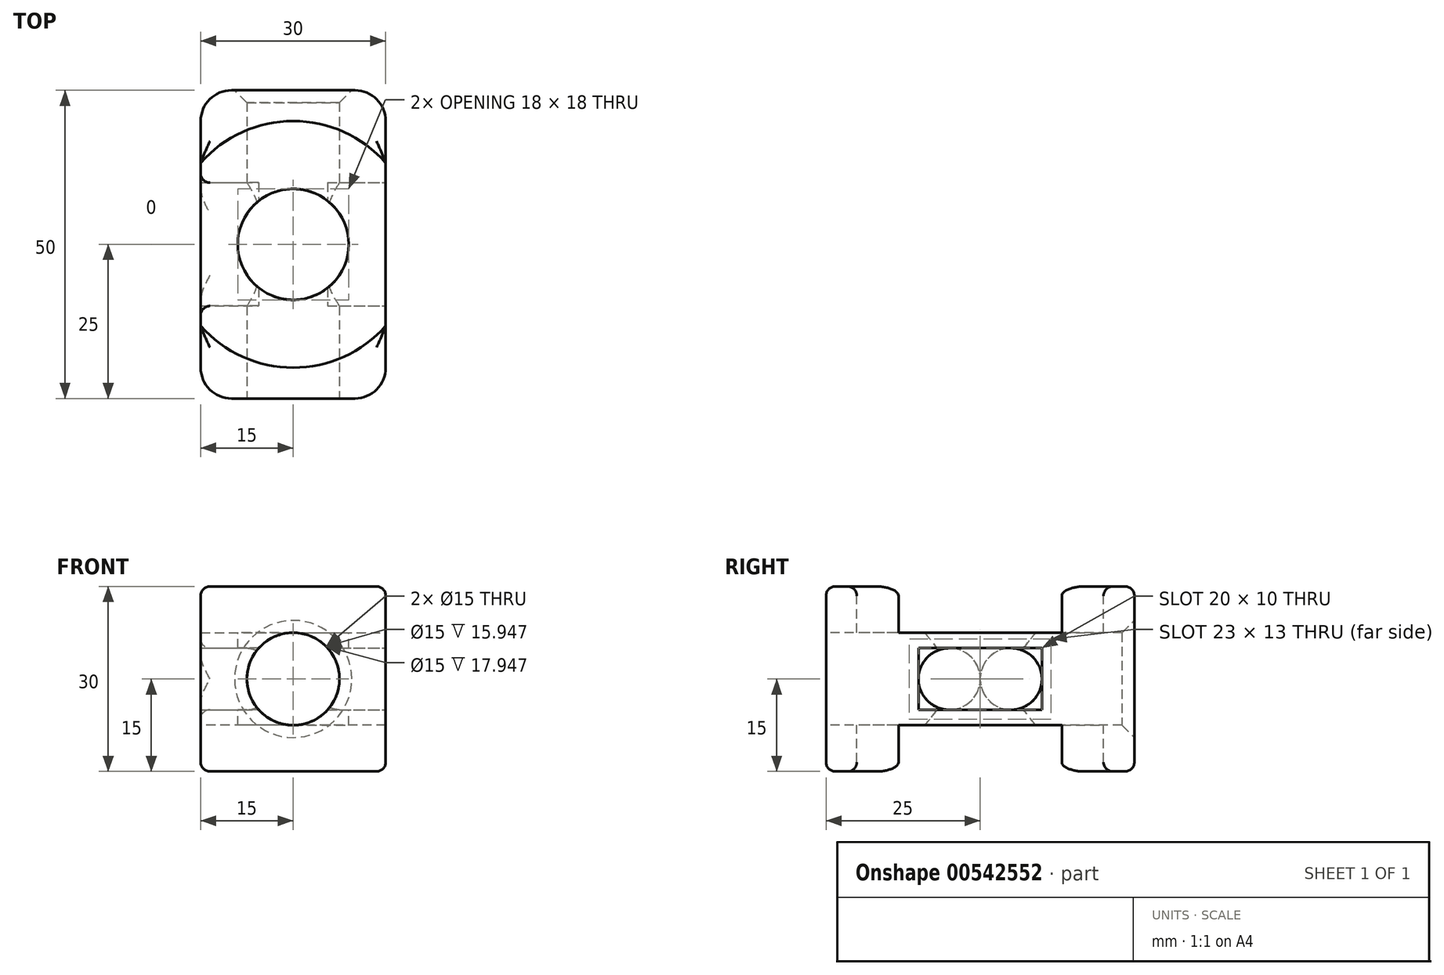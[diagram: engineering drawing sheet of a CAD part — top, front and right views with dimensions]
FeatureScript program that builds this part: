
annotation { "Feature Type Name" : "Feature", "Feature Type Description" : "" }
export const myFeature = defineFeature(function(context is Context, id is Id, definition is map)
    precondition{}
    {
        {
            var Q0;
            Q0=qCreatedBy(makeId("Right.planeOp"),FACE);
            var sketch = newSketch(context, id + "F0", { "sketchPlane" : qUnion([Q0])});
            skLineSegment(sketch, "E0.bottom", {"start": v(0, 15) * mm, "end": v(50, 15) * mm});
            skLineSegment(sketch, "E0.top", {"start": v(0, -15) * mm, "end": v(50, -15) * mm});
            skLineSegment(sketch, "E0.left", {"start": v(0, 15) * mm, "end": v(0, -15) * mm});
            skLineSegment(sketch, "E0.right", {"start": v(50, 15) * mm, "end": v(50, -15) * mm});
            skSolve(sketch);
        }
        {
            var Q0;
            Q0=makeQuery(id+"F0.imprint","IMPRINT",FACE,{"disambiguationData":[TD([[makeQuery(id+"F0.imprint","IMPRINT",EDGE,{"derivedFrom":sQuery(id+"F0.wireOp",EDGE,"E0.bottom")}),-1.0]])]});
            extrude(context, id + "F1", {"entities" : qUnion([Q0]), "endBound" : BoundingType.SYMMETRIC, "depth" : 30 * mm, "offsetDistance" : 25 * mm});
        }
        {
            var Q0;
            Q0=makeQuery(id+"F1.opExtrude","SWEPT_FACE",FACE,{"disambiguationData":[OSD([sQuery(id+"F0.wireOp",EDGE,"E0.left")])]});
            var sketch = newSketch(context, id + "F2", { "sketchPlane" : qUnion([Q0])});
            skCircle(sketch, "E1", {"center": v(0, 0) * mm, "radius": 7.5 * mm});
            skSolve(sketch);
        }
        {
            var Q0;
            Q0=makeQuery(id+"F1.opExtrude","CAP_FACE",FACE,{"disambiguationData":[OSD([sQuery(id+"F0.wireOp",EDGE,"E0.bottom"),sQuery(id+"F0.wireOp",EDGE,"E0.top"),sQuery(id+"F0.wireOp",EDGE,"E0.left"),sQuery(id+"F0.wireOp",EDGE,"E0.right")])],"isStart":false});
            var sketch = newSketch(context, id + "F3", { "sketchPlane" : qUnion([Q0])});
            skLineSegment(sketch, "E2.bottom", {"start": v(15, 5) * mm, "end": v(35, 5) * mm});
            skLineSegment(sketch, "E2.top", {"start": v(15, -5) * mm, "end": v(35, -5) * mm});
            skLineSegment(sketch, "E2.left", {"start": v(15, 5) * mm, "end": v(15, -5) * mm});
            skLineSegment(sketch, "E2.right", {"start": v(35, 5) * mm, "end": v(35, -5) * mm});
            skSolve(sketch);
        }
        {
            var Q0;
            Q0=makeQuery(id+"F3.imprint","IMPRINT",FACE,{"disambiguationData":[TD([[makeQuery(id+"F3.imprint","IMPRINT",EDGE,{"derivedFrom":sQuery(id+"F3.wireOp",EDGE,"E2.bottom")}),-1.0]])]});
            extrude(context, id + "F4", {"entities" : qUnion([Q0]), "operationType" : NewBodyOperationType.REMOVE, "endBound" : BoundingType.THROUGH_ALL, "oppositeDirection" : true, "depth" : 25 * mm, "offsetDistance" : 25 * mm});
        }
        {
            var Q0;
            Q0=makeQuery(id+"F2.imprint","IMPRINT",FACE,{"disambiguationData":[TD([[makeQuery(id+"F2.imprint","IMPRINT",EDGE,{"derivedFrom":sQuery(id+"F2.wireOp",EDGE,"E1")}),1.0]])]});
            extrude(context, id + "F5", {"entities" : qUnion([Q0]), "operationType" : NewBodyOperationType.REMOVE, "endBound" : BoundingType.THROUGH_ALL, "oppositeDirection" : true, "depth" : 25 * mm, "offsetDistance" : 25 * mm});
        }
        {
            var Q0;
            Q0=makeQuery(id+"F1.opExtrude","SWEPT_FACE",FACE,{"disambiguationData":[OSD([sQuery(id+"F0.wireOp",EDGE,"E0.bottom")])]});
            var sketch = newSketch(context, id + "F6", { "sketchPlane" : qUnion([Q0])});
            skLineSegment(sketch, "E3", {"start": v(15, 0) * mm, "end": v(-15, 50) * mm, "construction": true});
            skLineSegment(sketch, "E4", {"start": v(-15, 0) * mm, "end": v(15, 50) * mm, "construction": true});
            skCircle(sketch, "E5", {"center": v(0, 25) * mm, "radius": 20 * mm});
            skCircle(sketch, "E6", {"center": v(0, 25) * mm, "radius": 9 * mm});
            skSolve(sketch);
        }
        {
            var Q0;
            Q0=makeQuery(id+"F6.imprint","IMPRINT",FACE,{"disambiguationData":[TD([[makeQuery(id+"F6.imprint","IMPRINT",EDGE,{"derivedFrom":sQuery(id+"F6.wireOp",EDGE,"E6")}),1.0]])]});
            extrude(context, id + "F7", {"entities" : qUnion([Q0]), "operationType" : NewBodyOperationType.REMOVE, "endBound" : BoundingType.THROUGH_ALL, "oppositeDirection" : true, "depth" : 25 * mm, "offsetDistance" : 25 * mm});
        }
        {
            var Q0;
            Q0=makeQuery(id+"F6.imprint","IMPRINT",FACE,{"disambiguationData":[TD([[makeQuery(id+"F6.imprint","IMPRINT",EDGE,{"derivedFrom":sQuery(id+"F6.wireOp",EDGE,"E6")}),-1.0]])]});
            extrude(context, id + "F8", {"entities" : qUnion([Q0]), "operationType" : NewBodyOperationType.REMOVE, "oppositeDirection" : true, "depth" : 7.5 * mm, "offsetDistance" : 25 * mm});
        }
        {
            var Q0;
            Q0=makeQuery(id+"F6.imprint","IMPRINT",FACE,{"disambiguationData":[TD([[makeQuery(id+"F6.imprint","IMPRINT",EDGE,{"derivedFrom":sQuery(id+"F6.wireOp",EDGE,"E6")}),-1.0]])]});
            var Q1;
            Q1=makeQuery(id+"F1.opExtrude","SWEPT_FACE",FACE,{"disambiguationData":[OSD([sQuery(id+"F0.wireOp",EDGE,"E0.top")])]});
            extrude(context, id + "F9", {"entities" : qUnion([Q0]), "operationType" : NewBodyOperationType.REMOVE, "endBound" : BoundingType.UP_TO_SURFACE, "oppositeDirection" : true, "depth" : 25 * mm, "endBoundEntityFace" : qUnion([Q1]), "offsetDistance" : 25 * mm, "hasSecondDirection" : true, "secondDirectionOppositeDirection" : true, "secondDirectionDepth" : (30 - 7.5) * mm});
        }
        {
            var Q0;
            {var subQ0=sQuery(id+"F3.wireOp",EDGE,"E2.top");var subQ1=sQuery(id+"F3.wireOp",EDGE,"E2.right");Q0=makeQuery(id+"F5.boolean.opBoolean","SPLIT",EDGE,{"disambiguationData":[TD([makeQuery(id+"F1.opExtrude","CAP_FACE",FACE,{"disambiguationData":[OSD([sQuery(id+"F0.wireOp",EDGE,"E0.bottom"),sQuery(id+"F0.wireOp",EDGE,"E0.top"),sQuery(id+"F0.wireOp",EDGE,"E0.left"),sQuery(id+"F0.wireOp",EDGE,"E0.right")])],"isStart":false})])],"derivedFrom":makeQuery(id+"F4.boolean.opBoolean","COPY",EDGE,{"derivedFrom":makeQuery(id+"F4.opExtrude","SWEPT_EDGE",EDGE,{"disambiguationData":[OSD([subQ0,subQ1])]})})});}
            var Q1;
            {var subQ0=sQuery(id+"F3.wireOp",EDGE,"E2.top");var subQ1=sQuery(id+"F3.wireOp",EDGE,"E2.right");Q1=makeQuery(id+"F5.boolean.opBoolean","SPLIT",EDGE,{"disambiguationData":[TD([makeQuery(id+"F1.opExtrude","CAP_FACE",FACE,{"disambiguationData":[OSD([sQuery(id+"F0.wireOp",EDGE,"E0.bottom"),sQuery(id+"F0.wireOp",EDGE,"E0.top"),sQuery(id+"F0.wireOp",EDGE,"E0.left"),sQuery(id+"F0.wireOp",EDGE,"E0.right")])],"isStart":true})])],"derivedFrom":makeQuery(id+"F4.boolean.opBoolean","COPY",EDGE,{"derivedFrom":makeQuery(id+"F4.opExtrude","SWEPT_EDGE",EDGE,{"disambiguationData":[OSD([subQ0,subQ1])]})})});}
            var Q2;
            {var subQ0=sQuery(id+"F3.wireOp",EDGE,"E2.bottom");var subQ1=sQuery(id+"F3.wireOp",EDGE,"E2.right");Q2=makeQuery(id+"F5.boolean.opBoolean","SPLIT",EDGE,{"disambiguationData":[TD([makeQuery(id+"F1.opExtrude","CAP_FACE",FACE,{"disambiguationData":[OSD([sQuery(id+"F0.wireOp",EDGE,"E0.bottom"),sQuery(id+"F0.wireOp",EDGE,"E0.top"),sQuery(id+"F0.wireOp",EDGE,"E0.left"),sQuery(id+"F0.wireOp",EDGE,"E0.right")])],"isStart":false})])],"derivedFrom":makeQuery(id+"F4.boolean.opBoolean","COPY",EDGE,{"derivedFrom":makeQuery(id+"F4.opExtrude","SWEPT_EDGE",EDGE,{"disambiguationData":[OSD([subQ0,subQ1])]})})});}
            var Q3;
            {var subQ0=sQuery(id+"F3.wireOp",EDGE,"E2.bottom");var subQ1=sQuery(id+"F3.wireOp",EDGE,"E2.right");Q3=makeQuery(id+"F5.boolean.opBoolean","SPLIT",EDGE,{"disambiguationData":[TD([makeQuery(id+"F1.opExtrude","CAP_FACE",FACE,{"disambiguationData":[OSD([sQuery(id+"F0.wireOp",EDGE,"E0.bottom"),sQuery(id+"F0.wireOp",EDGE,"E0.top"),sQuery(id+"F0.wireOp",EDGE,"E0.left"),sQuery(id+"F0.wireOp",EDGE,"E0.right")])],"isStart":true})])],"derivedFrom":makeQuery(id+"F4.boolean.opBoolean","COPY",EDGE,{"derivedFrom":makeQuery(id+"F4.opExtrude","SWEPT_EDGE",EDGE,{"disambiguationData":[OSD([subQ0,subQ1])]})})});}
            var Q4;
            {var subQ0=sQuery(id+"F3.wireOp",EDGE,"E2.top");var subQ1=sQuery(id+"F3.wireOp",EDGE,"E2.left");Q4=makeQuery(id+"F5.boolean.opBoolean","SPLIT",EDGE,{"disambiguationData":[TD([makeQuery(id+"F1.opExtrude","CAP_FACE",FACE,{"disambiguationData":[OSD([sQuery(id+"F0.wireOp",EDGE,"E0.bottom"),sQuery(id+"F0.wireOp",EDGE,"E0.top"),sQuery(id+"F0.wireOp",EDGE,"E0.left"),sQuery(id+"F0.wireOp",EDGE,"E0.right")])],"isStart":true})])],"derivedFrom":makeQuery(id+"F4.boolean.opBoolean","COPY",EDGE,{"derivedFrom":makeQuery(id+"F4.opExtrude","SWEPT_EDGE",EDGE,{"disambiguationData":[OSD([subQ0,subQ1])]})})});}
            var Q5;
            {var subQ0=sQuery(id+"F3.wireOp",EDGE,"E2.bottom");var subQ1=sQuery(id+"F3.wireOp",EDGE,"E2.left");Q5=makeQuery(id+"F5.boolean.opBoolean","SPLIT",EDGE,{"disambiguationData":[TD([makeQuery(id+"F1.opExtrude","CAP_FACE",FACE,{"disambiguationData":[OSD([sQuery(id+"F0.wireOp",EDGE,"E0.bottom"),sQuery(id+"F0.wireOp",EDGE,"E0.top"),sQuery(id+"F0.wireOp",EDGE,"E0.left"),sQuery(id+"F0.wireOp",EDGE,"E0.right")])],"isStart":true})])],"derivedFrom":makeQuery(id+"F4.boolean.opBoolean","COPY",EDGE,{"derivedFrom":makeQuery(id+"F4.opExtrude","SWEPT_EDGE",EDGE,{"disambiguationData":[OSD([subQ0,subQ1])]})})});}
            var Q6;
            {var subQ0=sQuery(id+"F3.wireOp",EDGE,"E2.bottom");var subQ1=sQuery(id+"F3.wireOp",EDGE,"E2.left");Q6=makeQuery(id+"F5.boolean.opBoolean","SPLIT",EDGE,{"disambiguationData":[TD([makeQuery(id+"F1.opExtrude","CAP_FACE",FACE,{"disambiguationData":[OSD([sQuery(id+"F0.wireOp",EDGE,"E0.bottom"),sQuery(id+"F0.wireOp",EDGE,"E0.top"),sQuery(id+"F0.wireOp",EDGE,"E0.left"),sQuery(id+"F0.wireOp",EDGE,"E0.right")])],"isStart":false})])],"derivedFrom":makeQuery(id+"F4.boolean.opBoolean","COPY",EDGE,{"derivedFrom":makeQuery(id+"F4.opExtrude","SWEPT_EDGE",EDGE,{"disambiguationData":[OSD([subQ0,subQ1])]})})});}
            var Q7;
            {var subQ0=sQuery(id+"F3.wireOp",EDGE,"E2.top");var subQ1=sQuery(id+"F3.wireOp",EDGE,"E2.left");Q7=makeQuery(id+"F5.boolean.opBoolean","SPLIT",EDGE,{"disambiguationData":[TD([makeQuery(id+"F1.opExtrude","CAP_FACE",FACE,{"disambiguationData":[OSD([sQuery(id+"F0.wireOp",EDGE,"E0.bottom"),sQuery(id+"F0.wireOp",EDGE,"E0.top"),sQuery(id+"F0.wireOp",EDGE,"E0.left"),sQuery(id+"F0.wireOp",EDGE,"E0.right")])],"isStart":false})])],"derivedFrom":makeQuery(id+"F4.boolean.opBoolean","COPY",EDGE,{"derivedFrom":makeQuery(id+"F4.opExtrude","SWEPT_EDGE",EDGE,{"disambiguationData":[OSD([subQ0,subQ1])]})})});}
            fillet(context, id + "F10", {"entities" : qUnion([Q0, Q1, Q2, Q3, Q4, Q5, Q6, Q7]), "radius" : 5 * mm, "tangentPropagation" : true, "allowEdgeOverflow" : false});
        }
        {
            var Q0;
            Q0=makeQuery(id+"F5.boolean.opBoolean","INTERSECT",EDGE,{"derivedFrom":[makeQuery(id+"F1.opExtrude","SWEPT_FACE",FACE,{"disambiguationData":[OSD([sQuery(id+"F0.wireOp",EDGE,"E0.right")])]}),makeQuery(id+"F5.opExtrude","SWEPT_FACE",FACE,{"disambiguationData":[OSD([sQuery(id+"F2.wireOp",EDGE,"E1")])]})]});
            var Q1;
            Q1=makeQuery(id+"F5.boolean.opBoolean","COPY",EDGE,{"derivedFrom":makeQuery(id+"F5.opExtrude","CAP_EDGE",EDGE,{"disambiguationData":[OSD([sQuery(id+"F2.wireOp",EDGE,"E1")])],"isStart":true})});
            chamfer(context, id + "F11", {"entities" : qUnion([Q0, Q1]), "width" : 2 * mm, "tangentPropagation" : true});
        }
        {
            var Q0;
            Q0=makeQuery(id+"F1.opExtrude","CAP_EDGE",EDGE,{"disambiguationData":[OSD([sQuery(id+"F0.wireOp",EDGE,"E0.left")])],"isStart":true});
            var Q1;
            Q1=makeQuery(id+"F1.opExtrude","CAP_EDGE",EDGE,{"disambiguationData":[OSD([sQuery(id+"F0.wireOp",EDGE,"E0.left")])],"isStart":false});
            var Q2;
            Q2=makeQuery(id+"F1.opExtrude","CAP_EDGE",EDGE,{"disambiguationData":[OSD([sQuery(id+"F0.wireOp",EDGE,"E0.right")])],"isStart":true});
            var Q3;
            Q3=makeQuery(id+"F1.opExtrude","CAP_EDGE",EDGE,{"disambiguationData":[OSD([sQuery(id+"F0.wireOp",EDGE,"E0.right")])],"isStart":false});
            fillet(context, id + "F12", {"entities" : qUnion([Q0, Q1, Q2, Q3]), "radius" : 5 * mm, "tangentPropagation" : true, "allowEdgeOverflow" : false});
        }
        {
            var Q0;
            {var subQ0=sQuery(id+"F6.wireOp",EDGE,"E5");var subQ1=sQuery(id+"F0.wireOp",EDGE,"E0.bottom");var subQ2=makeQuery(id+"F1.opExtrude","CAP_EDGE",EDGE,{"disambiguationData":[OSD([subQ1])],"isStart":true});Q0=makeQuery(id+"F9.boolean.opBoolean","COPY",EDGE,{"derivedFrom":makeQuery(id+"F9.opExtrude","CAP_EDGE",EDGE,{"disambiguationData":[OSD([subQ1]),TDD([makeQuery(id+"F6.imprint","IMPRINT",EDGE,{"disambiguationData":[TD([[makeQuery(id+"F6.imprint","INTERSECT",VERTEX,{"disambiguationData":[OD(0.0)],"derivedFrom":[subQ2,subQ0]}),1.0]])],"derivedFrom":subQ2})])],"isStart":true})});}
            var Q1;
            {var subQ0=sQuery(id+"F6.wireOp",EDGE,"E5");var subQ1=sQuery(id+"F0.wireOp",EDGE,"E0.bottom");var subQ2=makeQuery(id+"F1.opExtrude","CAP_EDGE",EDGE,{"disambiguationData":[OSD([subQ1])],"isStart":false});Q1=makeQuery(id+"F9.boolean.opBoolean","COPY",EDGE,{"derivedFrom":makeQuery(id+"F9.opExtrude","CAP_EDGE",EDGE,{"disambiguationData":[OSD([subQ1]),TDD([makeQuery(id+"F6.imprint","IMPRINT",EDGE,{"disambiguationData":[TD([[makeQuery(id+"F6.imprint","INTERSECT",VERTEX,{"disambiguationData":[OD(0.0)],"derivedFrom":[subQ2,subQ0]}),1.0]])],"derivedFrom":subQ2})])],"isStart":true})});}
            var Q2;
            {var subQ0=sQuery(id+"F6.wireOp",EDGE,"E5");var subQ1=sQuery(id+"F0.wireOp",EDGE,"E0.bottom");var subQ2=makeQuery(id+"F1.opExtrude","CAP_EDGE",EDGE,{"disambiguationData":[OSD([subQ1])],"isStart":true});Q2=makeQuery(id+"F8.boolean.opBoolean","COPY",EDGE,{"derivedFrom":makeQuery(id+"F8.opExtrude","CAP_EDGE",EDGE,{"disambiguationData":[OSD([subQ1]),TDD([makeQuery(id+"F6.imprint","IMPRINT",EDGE,{"disambiguationData":[TD([[makeQuery(id+"F6.imprint","INTERSECT",VERTEX,{"disambiguationData":[OD(0.0)],"derivedFrom":[subQ2,subQ0]}),1.0]])],"derivedFrom":subQ2})])],"isStart":false})});}
            var Q3;
            {var subQ0=sQuery(id+"F6.wireOp",EDGE,"E5");var subQ1=sQuery(id+"F0.wireOp",EDGE,"E0.bottom");var subQ2=makeQuery(id+"F1.opExtrude","CAP_EDGE",EDGE,{"disambiguationData":[OSD([subQ1])],"isStart":false});Q3=makeQuery(id+"F8.boolean.opBoolean","COPY",EDGE,{"derivedFrom":makeQuery(id+"F8.opExtrude","CAP_EDGE",EDGE,{"disambiguationData":[OSD([subQ1]),TDD([makeQuery(id+"F6.imprint","IMPRINT",EDGE,{"disambiguationData":[TD([[makeQuery(id+"F6.imprint","INTERSECT",VERTEX,{"disambiguationData":[OD(0.0)],"derivedFrom":[subQ2,subQ0]}),1.0]])],"derivedFrom":subQ2})])],"isStart":false})});}
            var Q4;
            Q4=makeQuery(id+"F4.boolean.opBoolean","INTERSECT",EDGE,{"derivedFrom":[makeQuery(id+"F1.opExtrude","CAP_FACE",FACE,{"disambiguationData":[OSD([sQuery(id+"F0.wireOp",EDGE,"E0.bottom"),sQuery(id+"F0.wireOp",EDGE,"E0.top"),sQuery(id+"F0.wireOp",EDGE,"E0.left"),sQuery(id+"F0.wireOp",EDGE,"E0.right")])],"isStart":true}),makeQuery(id+"F4.opExtrude","SWEPT_FACE",FACE,{"disambiguationData":[OSD([sQuery(id+"F3.wireOp",EDGE,"E2.top")])]})]});
            var Q5;
            Q5=makeQuery(id+"F4.boolean.opBoolean","COPY",EDGE,{"derivedFrom":makeQuery(id+"F4.opExtrude","CAP_EDGE",EDGE,{"disambiguationData":[OSD([sQuery(id+"F3.wireOp",EDGE,"E2.top")])],"isStart":true})});
            var Q6;
            {var subQ1=sQuery(id+"F0.wireOp",EDGE,"E0.left");var subQ2=sQuery(id+"F0.wireOp",EDGE,"E0.top");Q6=makeQuery(id+"F9.boolean.opBoolean","SPLIT",FACE,{"disambiguationData":[TD([makeQuery(id+"F1.opExtrude","SWEPT_FACE",FACE,{"disambiguationData":[OSD([subQ1])]})])],"derivedFrom":makeQuery(id+"F1.opExtrude","SWEPT_FACE",FACE,{"disambiguationData":[OSD([subQ2])]})});}
            var Q7;
            {var subQ0=sQuery(id+"F0.wireOp",EDGE,"E0.right");var subQ2=sQuery(id+"F0.wireOp",EDGE,"E0.top");Q7=makeQuery(id+"F9.boolean.opBoolean","SPLIT",FACE,{"disambiguationData":[TD([makeQuery(id+"F1.opExtrude","SWEPT_FACE",FACE,{"disambiguationData":[OSD([subQ0])]})])],"derivedFrom":makeQuery(id+"F1.opExtrude","SWEPT_FACE",FACE,{"disambiguationData":[OSD([subQ2])]})});}
            var Q8;
            {var subQ1=sQuery(id+"F0.wireOp",EDGE,"E0.left");var subQ3=sQuery(id+"F0.wireOp",EDGE,"E0.bottom");Q8=makeQuery(id+"F8.boolean.opBoolean","SPLIT",FACE,{"disambiguationData":[TD([makeQuery(id+"F1.opExtrude","SWEPT_FACE",FACE,{"disambiguationData":[OSD([subQ1])]})])],"derivedFrom":makeQuery(id+"F1.opExtrude","SWEPT_FACE",FACE,{"disambiguationData":[OSD([subQ3])]})});}
            var Q9;
            {var subQ0=sQuery(id+"F0.wireOp",EDGE,"E0.right");var subQ3=sQuery(id+"F0.wireOp",EDGE,"E0.bottom");Q9=makeQuery(id+"F8.boolean.opBoolean","SPLIT",FACE,{"disambiguationData":[TD([makeQuery(id+"F1.opExtrude","SWEPT_FACE",FACE,{"disambiguationData":[OSD([subQ0])]})])],"derivedFrom":makeQuery(id+"F1.opExtrude","SWEPT_FACE",FACE,{"disambiguationData":[OSD([subQ3])]})});}
            var Q10;
            {var subQ0=sQuery(id+"F6.wireOp",EDGE,"E5");var subQ1=sQuery(id+"F0.wireOp",EDGE,"E0.bottom");Q10=makeQuery(id+"F8.boolean.opBoolean","COPY",EDGE,{"derivedFrom":makeQuery(id+"F8.opExtrude","SWEPT_EDGE",EDGE,{"disambiguationData":[OSD([subQ1,subQ0]),TDD([makeQuery(id+"F6.imprint","INTERSECT",VERTEX,{"disambiguationData":[OD(0.0)],"derivedFrom":[makeQuery(id+"F1.opExtrude","CAP_EDGE",EDGE,{"disambiguationData":[OSD([subQ1])],"isStart":false}),subQ0]})])]})});}
            var Q11;
            {var subQ0=sQuery(id+"F6.wireOp",EDGE,"E5");var subQ1=sQuery(id+"F0.wireOp",EDGE,"E0.bottom");Q11=makeQuery(id+"F8.boolean.opBoolean","COPY",EDGE,{"derivedFrom":makeQuery(id+"F8.opExtrude","SWEPT_EDGE",EDGE,{"disambiguationData":[OSD([subQ1,subQ0]),TDD([makeQuery(id+"F6.imprint","INTERSECT",VERTEX,{"disambiguationData":[OD(1.0)],"derivedFrom":[makeQuery(id+"F1.opExtrude","CAP_EDGE",EDGE,{"disambiguationData":[OSD([subQ1])],"isStart":false}),subQ0]})])]})});}
            var Q12;
            {var subQ0=sQuery(id+"F6.wireOp",EDGE,"E5");var subQ1=sQuery(id+"F0.wireOp",EDGE,"E0.bottom");Q12=makeQuery(id+"F8.boolean.opBoolean","COPY",EDGE,{"derivedFrom":makeQuery(id+"F8.opExtrude","SWEPT_EDGE",EDGE,{"disambiguationData":[OSD([subQ1,subQ0]),TDD([makeQuery(id+"F6.imprint","INTERSECT",VERTEX,{"disambiguationData":[OD(0.0)],"derivedFrom":[makeQuery(id+"F1.opExtrude","CAP_EDGE",EDGE,{"disambiguationData":[OSD([subQ1])],"isStart":true}),subQ0]})])]})});}
            var Q13;
            {var subQ0=sQuery(id+"F6.wireOp",EDGE,"E5");var subQ1=sQuery(id+"F0.wireOp",EDGE,"E0.bottom");Q13=makeQuery(id+"F8.boolean.opBoolean","COPY",EDGE,{"derivedFrom":makeQuery(id+"F8.opExtrude","SWEPT_EDGE",EDGE,{"disambiguationData":[OSD([subQ1,subQ0]),TDD([makeQuery(id+"F6.imprint","INTERSECT",VERTEX,{"disambiguationData":[OD(1.0)],"derivedFrom":[makeQuery(id+"F1.opExtrude","CAP_EDGE",EDGE,{"disambiguationData":[OSD([subQ1])],"isStart":true}),subQ0]})])]})});}
            var Q14;
            {var subQ0=sQuery(id+"F6.wireOp",EDGE,"E5");var subQ1=sQuery(id+"F0.wireOp",EDGE,"E0.bottom");Q14=makeQuery(id+"F9.boolean.opBoolean","COPY",EDGE,{"derivedFrom":makeQuery(id+"F9.opExtrude","SWEPT_EDGE",EDGE,{"disambiguationData":[OSD([subQ1,subQ0]),TDD([makeQuery(id+"F6.imprint","INTERSECT",VERTEX,{"disambiguationData":[OD(1.0)],"derivedFrom":[makeQuery(id+"F1.opExtrude","CAP_EDGE",EDGE,{"disambiguationData":[OSD([subQ1])],"isStart":true}),subQ0]})])]})});}
            var Q15;
            {var subQ0=sQuery(id+"F6.wireOp",EDGE,"E5");var subQ1=sQuery(id+"F0.wireOp",EDGE,"E0.bottom");Q15=makeQuery(id+"F9.boolean.opBoolean","COPY",EDGE,{"derivedFrom":makeQuery(id+"F9.opExtrude","SWEPT_EDGE",EDGE,{"disambiguationData":[OSD([subQ1,subQ0]),TDD([makeQuery(id+"F6.imprint","INTERSECT",VERTEX,{"disambiguationData":[OD(0.0)],"derivedFrom":[makeQuery(id+"F1.opExtrude","CAP_EDGE",EDGE,{"disambiguationData":[OSD([subQ1])],"isStart":true}),subQ0]})])]})});}
            var Q16;
            {var subQ0=sQuery(id+"F6.wireOp",EDGE,"E5");var subQ1=sQuery(id+"F0.wireOp",EDGE,"E0.bottom");Q16=makeQuery(id+"F9.boolean.opBoolean","COPY",EDGE,{"derivedFrom":makeQuery(id+"F9.opExtrude","SWEPT_EDGE",EDGE,{"disambiguationData":[OSD([subQ1,subQ0]),TDD([makeQuery(id+"F6.imprint","INTERSECT",VERTEX,{"disambiguationData":[OD(0.0)],"derivedFrom":[makeQuery(id+"F1.opExtrude","CAP_EDGE",EDGE,{"disambiguationData":[OSD([subQ1])],"isStart":false}),subQ0]})])]})});}
            var Q17;
            {var subQ0=sQuery(id+"F6.wireOp",EDGE,"E5");var subQ1=sQuery(id+"F0.wireOp",EDGE,"E0.bottom");Q17=makeQuery(id+"F9.boolean.opBoolean","COPY",EDGE,{"derivedFrom":makeQuery(id+"F9.opExtrude","SWEPT_EDGE",EDGE,{"disambiguationData":[OSD([subQ1,subQ0]),TDD([makeQuery(id+"F6.imprint","INTERSECT",VERTEX,{"disambiguationData":[OD(1.0)],"derivedFrom":[makeQuery(id+"F1.opExtrude","CAP_EDGE",EDGE,{"disambiguationData":[OSD([subQ1])],"isStart":false}),subQ0]})])]})});}
            fillet(context, id + "F13", {"entities" : qUnion([Q0, Q1, Q2, Q3, Q4, Q5, Q6, Q7, Q8, Q9, Q10, Q11, Q12, Q13, Q14, Q15, Q16, Q17]), "radius" : 1.5 * mm, "tangentPropagation" : true, "allowEdgeOverflow" : false});
        }
    });
